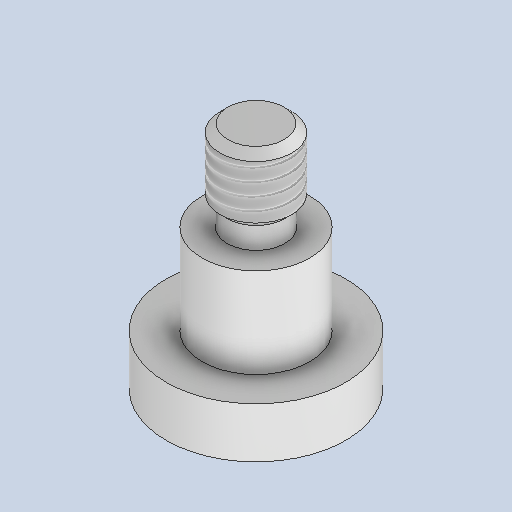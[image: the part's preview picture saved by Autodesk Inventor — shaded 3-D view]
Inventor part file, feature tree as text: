
AUTODESK INVENTOR PART (.ipt)
format: ipt  version: 2024.2 (Build 282272000, 272)  size: 299,520 bytes
history: native  units: mm
features: sketch x2, revolve x1, thread x1, extrude x1, chamfer x1
ambient origin geometry x8: Origin, YZ Plane, XZ Plane, XY Plane, X Axis, Y Axis, Z Axis, Center Point
bodies: Solid1 (feature_tree)
feature tree (6):
  revolve  "Revolution1"  [1 undecoded]
  thread  "Thread1"  [1 undecoded]
  extrude  "Extrusion1"  Depth=2.8mm
  chamfer  "Chamfer1"  Angle=90.0deg  [1 undecoded]
  sketch  "Sketch1"  dims[d0=10.0mm d1=6.0mm d2=4.0mm]
  sketch  "Sketch2"  dims[d4=5.0mm d5=2.8mm d6=90.0deg d7=6.0mm d8=0.0mm d9=2.5mm d10=2.0mm d11=0.0mm d12=0.43mm d13=2.0mm d14=45.0deg d15=5.0mm d16=3.2mm d17=1.2mm d18=45.0deg]
note: 3 required parameter values undecoded (feature->parameter linkage not recoverable at this tier; creation-order binding heuristic only, values carry confidence <= 0.55)